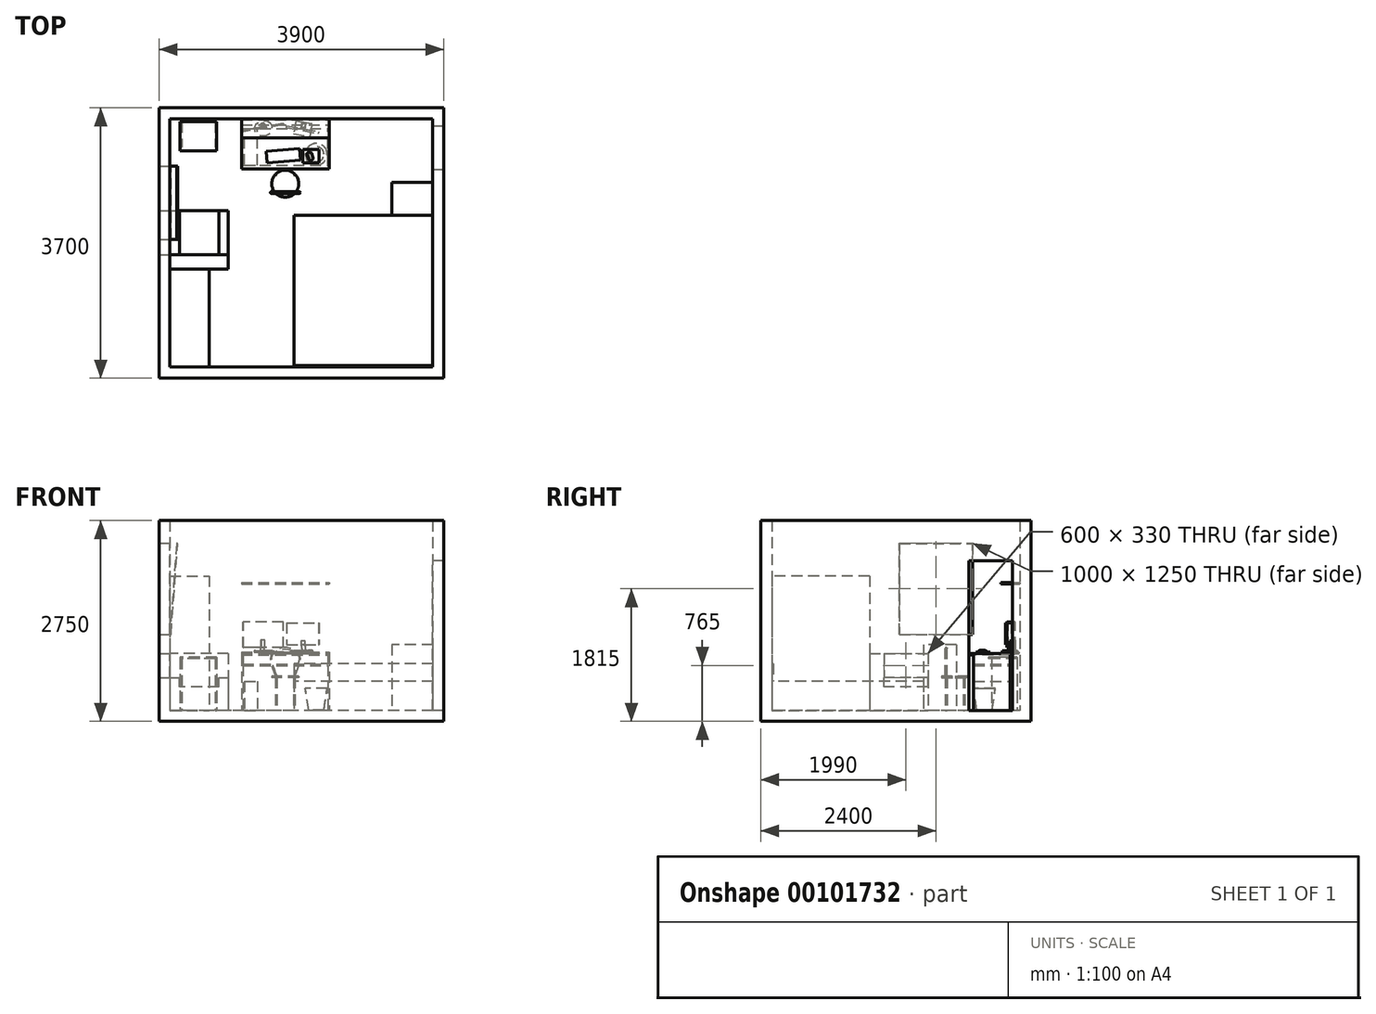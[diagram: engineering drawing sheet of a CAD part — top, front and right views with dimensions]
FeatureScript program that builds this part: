
annotation { "Feature Type Name" : "Feature", "Feature Type Description" : "" }
export const myFeature = defineFeature(function(context is Context, id is Id, definition is map)
    precondition{}
    {
        {
            var Q0;
            Q0=qCreatedBy(makeId("Top.planeOp"),FACE);
            var sketch = newSketch(context, id + "F0", { "sketchPlane" : qUnion([Q0])});
            skLineSegment(sketch, "E0.bottom", {"start": v(1800, 1700) * mm, "end": v(-1800, 1700) * mm});
            skLineSegment(sketch, "E0.top", {"start": v(1800, -1700) * mm, "end": v(-1800, -1700) * mm});
            skLineSegment(sketch, "E0.left", {"start": v(1800, 1700) * mm, "end": v(1800, -1700) * mm});
            skLineSegment(sketch, "E0.right", {"start": v(-1800, 1700) * mm, "end": v(-1800, -1700) * mm});
            skPoint(sketch, "E0.middle", {"position": v(0, 0) * mm});
            skLineSegment(sketch, "E1.0", {"start": v(-1950, 1850) * mm, "end": v(-1950, -1850) * mm});
            skLineSegment(sketch, "E1.1", {"start": v(1950, 1850) * mm, "end": v(-1950, 1850) * mm});
            skLineSegment(sketch, "E1.2", {"start": v(1950, 1850) * mm, "end": v(1950, -1850) * mm});
            skLineSegment(sketch, "E1.3", {"start": v(1950, -1850) * mm, "end": v(-1950, -1850) * mm});
            skSolve(sketch);
        }
        {
            var Q0;
            Q0 = qSketchRegion(id + "F0", true);
            var Q1;
            Q1=makeQuery(id+"F0.imprint","IMPRINT",FACE,{"disambiguationData":[TD([[makeQuery(id+"F0.imprint","IMPRINT",EDGE,{"derivedFrom":sQuery(id+"F0.wireOp",EDGE,"E0.bottom")}),1.0]])]});
            extrude(context, id + "F1", {"entities" : qUnion([Q0, Q1]), "oppositeDirection" : true, "depth" : 150 * mm});
        }
        {
            var Q0;
            Q0=makeQuery(id+"F0.imprint","IMPRINT",FACE,{"disambiguationData":[TD([[makeQuery(id+"F0.imprint","IMPRINT",EDGE,{"derivedFrom":sQuery(id+"F0.wireOp",EDGE,"E0.bottom")}),-1.0]])]});
            extrude(context, id + "F2", {"entities" : qUnion([Q0]), "operationType" : NewBodyOperationType.ADD, "depth" : 2600 * mm});
        }
        {
            var Q0;
            Q0=makeQuery(id+"F1.opExtrude","CAP_FACE",FACE,{"disambiguationData":[OSD([sQuery(id+"F0.wireOp",EDGE,"E1.0"),sQuery(id+"F0.wireOp",EDGE,"E1.1"),sQuery(id+"F0.wireOp",EDGE,"E1.2"),sQuery(id+"F0.wireOp",EDGE,"E1.3")])],"isStart":true});
            var sketch = newSketch(context, id + "F3", { "sketchPlane" : qUnion([Q0])});
            skLineSegment(sketch, "E2.bottom", {"start": v(1800, -1700) * mm, "end": v(-100, -1700) * mm});
            skLineSegment(sketch, "E2.top", {"start": v(1800, 380) * mm, "end": v(-100, 380) * mm});
            skLineSegment(sketch, "E2.left", {"start": v(1800, -1700) * mm, "end": v(1800, 380) * mm});
            skLineSegment(sketch, "E2.right", {"start": v(-100, -1700) * mm, "end": v(-100, 380) * mm});
            skSolve(sketch);
        }
        {
            var Q0;
            Q0 = qSketchRegion(id + "F3", true);
            extrude(context, id + "F4", {"entities" : qUnion([Q0]), "depth" : 400 * mm});
        }
        {
            var Q0;
            Q0=makeQuery(id+"F1.opExtrude","CAP_FACE",FACE,{"disambiguationData":[OSD([sQuery(id+"F0.wireOp",EDGE,"E1.0"),sQuery(id+"F0.wireOp",EDGE,"E1.1"),sQuery(id+"F0.wireOp",EDGE,"E1.2"),sQuery(id+"F0.wireOp",EDGE,"E1.3")])],"isStart":true});
            var sketch = newSketch(context, id + "F5", { "sketchPlane" : qUnion([Q0])});
            skLineSegment(sketch, "E3.bottom", {"start": v(-1800, -1700) * mm, "end": v(-1260, -1700) * mm});
            skLineSegment(sketch, "E3.top", {"start": v(-1800, -360) * mm, "end": v(-1260, -360) * mm});
            skLineSegment(sketch, "E3.left", {"start": v(-1800, -1700) * mm, "end": v(-1800, -360) * mm});
            skLineSegment(sketch, "E3.right", {"start": v(-1260, -1700) * mm, "end": v(-1260, -360) * mm});
            skSolve(sketch);
        }
        {
            var Q0;
            Q0 = qSketchRegion(id + "F5", true);
            extrude(context, id + "F6", {"entities" : qUnion([Q0]), "depth" : 1840 * mm});
        }
        {
            var Q0;
            Q0=makeQuery(id+"F1.opExtrude","CAP_FACE",FACE,{"disambiguationData":[OSD([sQuery(id+"F0.wireOp",EDGE,"E1.0"),sQuery(id+"F0.wireOp",EDGE,"E1.1"),sQuery(id+"F0.wireOp",EDGE,"E1.2"),sQuery(id+"F0.wireOp",EDGE,"E1.3")])],"isStart":true});
            var sketch = newSketch(context, id + "F7", { "sketchPlane" : qUnion([Q0])});
            skLineSegment(sketch, "E4.bottom", {"start": v(1800, 380) * mm, "end": v(1240, 380) * mm});
            skLineSegment(sketch, "E4.top", {"start": v(1800, 830) * mm, "end": v(1240, 830) * mm});
            skLineSegment(sketch, "E4.left", {"start": v(1800, 380) * mm, "end": v(1800, 830) * mm});
            skLineSegment(sketch, "E4.right", {"start": v(1240, 380) * mm, "end": v(1240, 830) * mm});
            skSolve(sketch);
        }
        {
            var Q0;
            Q0 = qSketchRegion(id + "F7", true);
            extrude(context, id + "F8", {"entities" : qUnion([Q0]), "depth" : 900 * mm});
        }
        {
            var Q0;
            Q0=makeQuery(id+"F1.opExtrude","CAP_FACE",FACE,{"disambiguationData":[OSD([sQuery(id+"F0.wireOp",EDGE,"E1.0"),sQuery(id+"F0.wireOp",EDGE,"E1.1"),sQuery(id+"F0.wireOp",EDGE,"E1.2"),sQuery(id+"F0.wireOp",EDGE,"E1.3")])],"isStart":true});
            var sketch = newSketch(context, id + "F9", { "sketchPlane" : qUnion([Q0])});
            skLineSegment(sketch, "E5.bottom", {"start": v(-1000, -360) * mm, "end": v(-1800, -360) * mm});
            skLineSegment(sketch, "E5.top", {"start": v(-1000, 440) * mm, "end": v(-1800, 440) * mm});
            skLineSegment(sketch, "E5.left", {"start": v(-1000, -360) * mm, "end": v(-1000, 440) * mm});
            skLineSegment(sketch, "E5.right", {"start": v(-1800, -360) * mm, "end": v(-1800, 440) * mm});
            skSolve(sketch);
        }
        {
            var Q0;
            Q0 = qSketchRegion(id + "F9", true);
            extrude(context, id + "F10", {"entities" : qUnion([Q0]), "depth" : 780 * mm});
        }
        {
            var Q0;
            Q0=makeQuery(id+"F10.opExtrude","CAP_FACE",FACE,{"disambiguationData":[OSD([sQuery(id+"F9.wireOp",EDGE,"E5.bottom"),sQuery(id+"F9.wireOp",EDGE,"E5.top"),sQuery(id+"F9.wireOp",EDGE,"E5.left"),sQuery(id+"F9.wireOp",EDGE,"E5.right")])],"isStart":false});
            var sketch = newSketch(context, id + "F11", { "sketchPlane" : qUnion([Q0])});
            skLineSegment(sketch, "E6.bottom", {"start": v(-1670, 440) * mm, "end": v(-1130, 440) * mm});
            skLineSegment(sketch, "E6.top", {"start": v(-1670, -160) * mm, "end": v(-1130, -160) * mm});
            skLineSegment(sketch, "E6.left", {"start": v(-1670, 440) * mm, "end": v(-1670, -160) * mm});
            skLineSegment(sketch, "E6.right", {"start": v(-1130, 440) * mm, "end": v(-1130, -160) * mm});
            skSolve(sketch);
        }
        {
            var Q0;
            Q0 = qSketchRegion(id + "F11", true);
            extrude(context, id + "F12", {"entities" : qUnion([Q0]), "operationType" : NewBodyOperationType.REMOVE, "oppositeDirection" : true, "depth" : 460 * mm});
        }
        {
            var Q0;
            Q0=makeQuery(id+"F12.boolean.opBoolean","COPY",FACE,{"derivedFrom":makeQuery(id+"F12.opExtrude","SWEPT_FACE",FACE,{"disambiguationData":[OSD([sQuery(id+"F11.wireOp",EDGE,"E6.left")])]})});
            var sketch = newSketch(context, id + "F13", { "sketchPlane" : qUnion([Q0])});
            skLineSegment(sketch, "E7.bottom", {"start": v(-160, 780) * mm, "end": v(440, 780) * mm});
            skLineSegment(sketch, "E7.top", {"start": v(-160, 450) * mm, "end": v(440, 450) * mm});
            skLineSegment(sketch, "E7.left", {"start": v(-160, 780) * mm, "end": v(-160, 450) * mm});
            skLineSegment(sketch, "E7.right", {"start": v(440, 780) * mm, "end": v(440, 450) * mm});
            skSolve(sketch);
        }
        {
            var Q0;
            Q0 = qSketchRegion(id + "F13", true);
            extrude(context, id + "F14", {"entities" : qUnion([Q0]), "operationType" : NewBodyOperationType.REMOVE, "oppositeDirection" : true, "depth" : 3679.97 * mm, "symmetric" : true});
        }
        {
            var Q0;
            Q0=makeQuery(id+"F2.opExtrude","SWEPT_FACE",FACE,{"disambiguationData":[OSD([sQuery(id+"F0.wireOp",EDGE,"E0.left")])]});
            var sketch = newSketch(context, id + "F15", { "sketchPlane" : qUnion([Q0])});
            skLineSegment(sketch, "E8.bottom", {"start": v(-1600, 0) * mm, "end": v(-1000, 0) * mm});
            skLineSegment(sketch, "E8.top", {"start": v(-1600, 2050) * mm, "end": v(-1000, 2050) * mm});
            skLineSegment(sketch, "E8.left", {"start": v(-1600, 0) * mm, "end": v(-1600, 2050) * mm});
            skLineSegment(sketch, "E8.right", {"start": v(-1000, 0) * mm, "end": v(-1000, 2050) * mm});
            skSolve(sketch);
        }
        {
            var Q0;
            Q0 = qSketchRegion(id + "F15", true);
            extrude(context, id + "F16", {"entities" : qUnion([Q0]), "operationType" : NewBodyOperationType.REMOVE, "oppositeDirection" : true, "depth" : 500 * mm});
        }
        {
            var Q0;
            Q0=makeQuery(id+"F16.boolean.opBoolean","MERGE",FACE,{"derivedFrom":[makeQuery(id+"F1.opExtrude","CAP_FACE",FACE,{"disambiguationData":[OSD([sQuery(id+"F0.wireOp",EDGE,"E1.0"),sQuery(id+"F0.wireOp",EDGE,"E1.1"),sQuery(id+"F0.wireOp",EDGE,"E1.2"),sQuery(id+"F0.wireOp",EDGE,"E1.3")])],"isStart":true}),makeQuery(id+"F16.opExtrude","SWEPT_FACE",FACE,{"disambiguationData":[OSD([sQuery(id+"F15.wireOp",EDGE,"E8.bottom")])]})]});
            var sketch = newSketch(context, id + "F17", { "sketchPlane" : qUnion([Q0])});
            skLineSegment(sketch, "E9.bottom", {"start": v(380, 1565) * mm, "end": v(360, 1565) * mm});
            skLineSegment(sketch, "E9.top", {"start": v(380, 1065) * mm, "end": v(360, 1065) * mm});
            skLineSegment(sketch, "E9.left", {"start": v(380, 1565) * mm, "end": v(380, 1065) * mm});
            skLineSegment(sketch, "E9.right", {"start": v(360, 1565) * mm, "end": v(360, 1065) * mm});
            skLineSegment(sketch, "E10.bottom", {"start": v(-800, 1565) * mm, "end": v(-820, 1565) * mm});
            skLineSegment(sketch, "E10.top", {"start": v(-800, 1065) * mm, "end": v(-820, 1065) * mm});
            skLineSegment(sketch, "E10.left", {"start": v(-800, 1565) * mm, "end": v(-800, 1065) * mm});
            skLineSegment(sketch, "E10.right", {"start": v(-820, 1565) * mm, "end": v(-820, 1065) * mm});
            skSolve(sketch);
        }
        {
            var Q0;
            Q0 = qSketchRegion(id + "F17", true);
            extrude(context, id + "F18", {"entities" : qUnion([Q0]), "depth" : 760 * mm});
        }
        {
            var Q0;
            Q0=makeQuery(id+"F18.opExtrude","CAP_FACE",FACE,{"disambiguationData":[OSD([sQuery(id+"F17.wireOp",EDGE,"E10.bottom"),sQuery(id+"F17.wireOp",EDGE,"E10.top"),sQuery(id+"F17.wireOp",EDGE,"E10.left"),sQuery(id+"F17.wireOp",EDGE,"E10.right")])],"isStart":false});
            var sketch = newSketch(context, id + "F19", { "sketchPlane" : qUnion([Q0])});
            skLineSegment(sketch, "E11.bottom", {"start": v(-820, 1615) * mm, "end": v(380, 1615) * mm});
            skLineSegment(sketch, "E11.top", {"start": v(-820, 1015) * mm, "end": v(380, 1015) * mm});
            skLineSegment(sketch, "E11.left", {"start": v(-820, 1615) * mm, "end": v(-820, 1015) * mm});
            skLineSegment(sketch, "E11.right", {"start": v(380, 1615) * mm, "end": v(380, 1015) * mm});
            skSolve(sketch);
        }
        {
            var Q0;
            Q0 = qSketchRegion(id + "F19", true);
            extrude(context, id + "F20", {"entities" : qUnion([Q0]), "operationType" : NewBodyOperationType.ADD, "depth" : 20 * mm});
        }
        {
            var Q0;
            Q0=makeQuery(id+"F20.opExtrude","CAP_FACE",FACE,{"disambiguationData":[OSD([sQuery(id+"F19.wireOp",EDGE,"E11.bottom"),sQuery(id+"F19.wireOp",EDGE,"E11.top"),sQuery(id+"F19.wireOp",EDGE,"E11.left"),sQuery(id+"F19.wireOp",EDGE,"E11.right")])],"isStart":true});
            cPlane(context, id + "F21", {"entities" : qUnion([Q0]), "cplaneType" : CPlaneType.OFFSET, "offset" : 125 * mm, "width" : 150 * mm, "height" : 150 * mm});
        }
        {
            var Q0;
            Q0=qCreatedBy(id+"F21.planeOp",FACE);
            var sketch = newSketch(context, id + "F22", { "sketchPlane" : qUnion([Q0])});
            skLineSegment(sketch, "E12.bottom", {"start": v(-800, -1065) * mm, "end": v(360, -1065) * mm});
            skLineSegment(sketch, "E12.top", {"start": v(-800, -1565) * mm, "end": v(360, -1565) * mm});
            skLineSegment(sketch, "E12.left", {"start": v(-800, -1065) * mm, "end": v(-800, -1565) * mm});
            skLineSegment(sketch, "E12.right", {"start": v(360, -1065) * mm, "end": v(360, -1565) * mm});
            skSolve(sketch);
        }
        {
            var Q0;
            Q0 = qSketchRegion(id + "F22", true);
            extrude(context, id + "F23", {"entities" : qUnion([Q0]), "operationType" : NewBodyOperationType.ADD, "depth" : 20 * mm});
        }
        {
            var Q0;
            Q0=makeQuery(id+"F20.opExtrude","CAP_FACE",FACE,{"disambiguationData":[OSD([sQuery(id+"F19.wireOp",EDGE,"E11.bottom"),sQuery(id+"F19.wireOp",EDGE,"E11.top"),sQuery(id+"F19.wireOp",EDGE,"E11.left"),sQuery(id+"F19.wireOp",EDGE,"E11.right")])],"isStart":false});
            var sketch = newSketch(context, id + "F24", { "sketchPlane" : qUnion([Q0])});
            skLineSegment(sketch, "E13.bottom", {"start": v(-820, 1440) * mm, "end": v(380, 1440) * mm});
            skLineSegment(sketch, "E13.top", {"start": v(-820, 1690) * mm, "end": v(380, 1690) * mm});
            skLineSegment(sketch, "E13.left", {"start": v(-820, 1440) * mm, "end": v(-820, 1690) * mm});
            skLineSegment(sketch, "E13.right", {"start": v(380, 1440) * mm, "end": v(380, 1690) * mm});
            skSolve(sketch);
        }
        {
            var Q0;
            Q0 = qSketchRegion(id + "F24", true);
            extrude(context, id + "F25", {"entities" : qUnion([Q0]), "operationType" : NewBodyOperationType.ADD, "depth" : 20 * mm});
        }
        {
            var Q0;
            Q0=makeQuery(id+"F16.boolean.opBoolean","MERGE",FACE,{"derivedFrom":[makeQuery(id+"F1.opExtrude","CAP_FACE",FACE,{"disambiguationData":[OSD([sQuery(id+"F0.wireOp",EDGE,"E1.0"),sQuery(id+"F0.wireOp",EDGE,"E1.1"),sQuery(id+"F0.wireOp",EDGE,"E1.2"),sQuery(id+"F0.wireOp",EDGE,"E1.3")])],"isStart":true}),makeQuery(id+"F16.opExtrude","SWEPT_FACE",FACE,{"disambiguationData":[OSD([sQuery(id+"F15.wireOp",EDGE,"E8.bottom")])]})]});
            var sketch = newSketch(context, id + "F26", { "sketchPlane" : qUnion([Q0])});
            skLineSegment(sketch, "E14.bottom", {"start": v(-1180, 1660) * mm, "end": v(-1160, 1660) * mm});
            skLineSegment(sketch, "E14.top", {"start": v(-1180, 1315) * mm, "end": v(-1160, 1315) * mm});
            skLineSegment(sketch, "E14.left", {"start": v(-1180, 1660) * mm, "end": v(-1180, 1315) * mm});
            skLineSegment(sketch, "E14.right", {"start": v(-1160, 1660) * mm, "end": v(-1160, 1315) * mm});
            skLineSegment(sketch, "E15.bottom", {"start": v(-1660, 1660) * mm, "end": v(-1640, 1660) * mm});
            skLineSegment(sketch, "E15.top", {"start": v(-1660, 1315) * mm, "end": v(-1640, 1315) * mm});
            skLineSegment(sketch, "E15.left", {"start": v(-1660, 1660) * mm, "end": v(-1660, 1315) * mm});
            skLineSegment(sketch, "E15.right", {"start": v(-1640, 1660) * mm, "end": v(-1640, 1315) * mm});
            skSolve(sketch);
        }
        {
            var Q0;
            Q0 = qSketchRegion(id + "F26", true);
            extrude(context, id + "F27", {"entities" : qUnion([Q0]), "depth" : 710 * mm});
        }
        {
            var Q0;
            Q0=makeQuery(id+"F4.opExtrude","CAP_FACE",FACE,{"disambiguationData":[OSD([sQuery(id+"F3.wireOp",EDGE,"E2.bottom"),sQuery(id+"F3.wireOp",EDGE,"E2.top"),sQuery(id+"F3.wireOp",EDGE,"E2.left"),sQuery(id+"F3.wireOp",EDGE,"E2.right")])],"isStart":false});
            var sketch = newSketch(context, id + "F28", { "sketchPlane" : qUnion([Q0])});
            skLineSegment(sketch, "E16.bottom", {"start": v(1800, -1700) * mm, "end": v(-100, -1700) * mm});
            skLineSegment(sketch, "E16.top", {"start": v(1800, -1680) * mm, "end": v(-100, -1680) * mm});
            skLineSegment(sketch, "E16.left", {"start": v(1800, -1700) * mm, "end": v(1800, -1680) * mm});
            skLineSegment(sketch, "E16.right", {"start": v(-100, -1700) * mm, "end": v(-100, -1680) * mm});
            skSolve(sketch);
        }
        {
            var Q0;
            Q0 = qSketchRegion(id + "F28", true);
            extrude(context, id + "F29", {"entities" : qUnion([Q0]), "operationType" : NewBodyOperationType.ADD, "depth" : 240 * mm});
        }
        {
            var Q0;
            Q0=makeQuery(id+"F27.opExtrude","CAP_FACE",FACE,{"disambiguationData":[OSD([sQuery(id+"F26.wireOp",EDGE,"E14.bottom"),sQuery(id+"F26.wireOp",EDGE,"E14.top"),sQuery(id+"F26.wireOp",EDGE,"E14.left"),sQuery(id+"F26.wireOp",EDGE,"E14.right")])],"isStart":false});
            var sketch = newSketch(context, id + "F30", { "sketchPlane" : qUnion([Q0])});
            skLineSegment(sketch, "E17.bottom", {"start": v(-1160, 1660) * mm, "end": v(-1660, 1660) * mm});
            skLineSegment(sketch, "E17.top", {"start": v(-1160, 1265) * mm, "end": v(-1660, 1265) * mm});
            skLineSegment(sketch, "E17.left", {"start": v(-1160, 1660) * mm, "end": v(-1160, 1265) * mm});
            skLineSegment(sketch, "E17.right", {"start": v(-1660, 1660) * mm, "end": v(-1660, 1265) * mm});
            skSolve(sketch);
        }
        {
            var Q0;
            Q0 = qSketchRegion(id + "F30", true);
            extrude(context, id + "F31", {"entities" : qUnion([Q0]), "operationType" : NewBodyOperationType.ADD, "depth" : 20 * mm});
        }
        {
            var Q0;
            Q0=makeQuery(id+"F2.opExtrude","SWEPT_FACE",FACE,{"disambiguationData":[OSD([sQuery(id+"F0.wireOp",EDGE,"E0.bottom")])]});
            var sketch = newSketch(context, id + "F32", { "sketchPlane" : qUnion([Q0])});
            skLineSegment(sketch, "E18.bottom", {"start": v(-820, 1750) * mm, "end": v(380, 1750) * mm});
            skLineSegment(sketch, "E18.top", {"start": v(-820, 1730) * mm, "end": v(380, 1730) * mm});
            skLineSegment(sketch, "E18.left", {"start": v(-820, 1750) * mm, "end": v(-820, 1730) * mm});
            skLineSegment(sketch, "E18.right", {"start": v(380, 1750) * mm, "end": v(380, 1730) * mm});
            skSolve(sketch);
        }
        {
            var Q0;
            Q0 = qSketchRegion(id + "F32", true);
            extrude(context, id + "F33", {"entities" : qUnion([Q0]), "depth" : 260 * mm});
        }
        {
            var Q0;
            Q0=makeQuery(id+"F2.opExtrude","SWEPT_FACE",FACE,{"disambiguationData":[OSD([sQuery(id+"F0.wireOp",EDGE,"E0.right")])]});
            var sketch = newSketch(context, id + "F34", { "sketchPlane" : qUnion([Q0])});
            skLineSegment(sketch, "E19.bottom", {"start": v(1050, 1040) * mm, "end": v(50, 1040) * mm});
            skLineSegment(sketch, "E19.top", {"start": v(1050, 2290) * mm, "end": v(50, 2290) * mm});
            skLineSegment(sketch, "E19.left", {"start": v(1050, 1040) * mm, "end": v(1050, 2290) * mm});
            skLineSegment(sketch, "E19.right", {"start": v(50, 1040) * mm, "end": v(50, 2290) * mm});
            skSolve(sketch);
        }
        {
            var Q0;
            Q0 = qSketchRegion(id + "F34", true);
            extrude(context, id + "F35", {"entities" : qUnion([Q0]), "operationType" : NewBodyOperationType.REMOVE, "oppositeDirection" : true, "depth" : 500 * mm});
        }
        {
            var Q0;
            Q0=makeQuery(id+"F2.opExtrude","CAP_FACE",FACE,{"disambiguationData":[OSD([sQuery(id+"F0.wireOp",EDGE,"E0.bottom"),sQuery(id+"F0.wireOp",EDGE,"E0.top"),sQuery(id+"F0.wireOp",EDGE,"E0.left"),sQuery(id+"F0.wireOp",EDGE,"E0.right"),sQuery(id+"F0.wireOp",EDGE,"E1.0"),sQuery(id+"F0.wireOp",EDGE,"E1.1"),sQuery(id+"F0.wireOp",EDGE,"E1.2"),sQuery(id+"F0.wireOp",EDGE,"E1.3")])],"isStart":false});
            var sketch = newSketch(context, id + "F36", { "sketchPlane" : qUnion([Q0])});
            skLineSegment(sketch, "E20.0", {"start": v(-1950, 1850) * mm, "end": v(-1950, -1850) * mm});
            skLineSegment(sketch, "E20.1", {"start": v(1950, -1850) * mm, "end": v(-1950, -1850) * mm});
            skLineSegment(sketch, "E20.2", {"start": v(1950, 1850) * mm, "end": v(1950, -1850) * mm});
            skLineSegment(sketch, "E20.3", {"start": v(1950, 1850) * mm, "end": v(-1950, 1850) * mm});
            skSolve(sketch);
        }
        {
            var Q0;
            Q0=makeQuery(id+"F35.boolean.opBoolean","COPY",FACE,{"derivedFrom":makeQuery(id+"F35.opExtrude","SWEPT_FACE",FACE,{"disambiguationData":[OSD([sQuery(id+"F34.wireOp",EDGE,"E19.left")])]})});
            var sketch = newSketch(context, id + "F37", { "sketchPlane" : qUnion([Q0])});
            skLineSegment(sketch, "E21", {"start": v(-1800, 1040) * mm, "end": v(-1710, 2286.76) * mm});
            skLineSegment(sketch, "E22", {"start": v(-1710, 2286.76) * mm, "end": v(-1695.04, 2285.68) * mm});
            skLineSegment(sketch, "E23", {"start": v(-1695.04, 2285.68) * mm, "end": v(-1785.04, 1038.92) * mm});
            skLineSegment(sketch, "E24", {"start": v(-1785.04, 1038.92) * mm, "end": v(-1800, 1040) * mm});
            skSolve(sketch);
        }
        {
            var Q0;
            Q0 = qSketchRegion(id + "F37", true);
            var Q1;
            Q1=makeQuery(id+"F35.boolean.opBoolean","COPY",FACE,{"derivedFrom":makeQuery(id+"F35.opExtrude","SWEPT_FACE",FACE,{"disambiguationData":[OSD([sQuery(id+"F34.wireOp",EDGE,"E19.right")])]})});
            extrude(context, id + "F38", {"entities" : qUnion([Q0]), "endBound" : BoundingType.UP_TO_SURFACE, "endBoundEntityFace" : qUnion([Q1]), "depth" : 25 * mm});
        }
        {
            var Q0;
            Q0=makeQuery(id+"F16.boolean.opBoolean","MERGE",FACE,{"derivedFrom":[makeQuery(id+"F1.opExtrude","CAP_FACE",FACE,{"disambiguationData":[OSD([sQuery(id+"F0.wireOp",EDGE,"E1.0"),sQuery(id+"F0.wireOp",EDGE,"E1.1"),sQuery(id+"F0.wireOp",EDGE,"E1.2"),sQuery(id+"F0.wireOp",EDGE,"E1.3")])],"isStart":true}),makeQuery(id+"F16.opExtrude","SWEPT_FACE",FACE,{"disambiguationData":[OSD([sQuery(id+"F15.wireOp",EDGE,"E8.bottom")])]})]});
            var sketch = newSketch(context, id + "F39", { "sketchPlane" : qUnion([Q0])});
            skCircle(sketch, "E25", {"center": v(-342.5, 935) * mm, "radius": 10 * mm});
            skCircle(sketch, "E26", {"center": v(-97.5, 935) * mm, "radius": 10 * mm});
            skCircle(sketch, "E27", {"center": v(-97.5, 690) * mm, "radius": 10 * mm});
            skCircle(sketch, "E28", {"center": v(-342.5, 690) * mm, "radius": 10 * mm});
            skLineSegment(sketch, "E29", {"start": v(-97.5, 935) * mm, "end": v(-342.5, 935) * mm, "construction": true});
            skLineSegment(sketch, "E30", {"start": v(-220, 935) * mm, "end": v(-220, 690) * mm, "construction": true});
            skLineSegment(sketch, "E31", {"start": v(-97.5, 690) * mm, "end": v(-342.5, 690) * mm, "construction": true});
            skLineSegment(sketch, "E32", {"start": v(-220, 935) * mm, "end": v(-220, 1015) * mm, "construction": true});
            skSolve(sketch);
        }
        {
            var Q0;
            Q0 = qSketchRegion(id + "F39", true);
            extrude(context, id + "F40", {"entities" : qUnion([Q0]), "depth" : 450 * mm});
        }
        {
            var Q0;
            Q0=makeQuery(id+"F40.opExtrude","CAP_FACE",FACE,{"disambiguationData":[OSD([sQuery(id+"F39.wireOp",EDGE,"E27")])],"isStart":false});
            var sketch = newSketch(context, id + "F41", { "sketchPlane" : qUnion([Q0])});
            skCircle(sketch, "E33", {"center": v(-220, 812.5) * mm, "radius": 185 * mm});
            skSolve(sketch);
        }
        {
            var Q0;
            Q0 = qSketchRegion(id + "F41", true);
            extrude(context, id + "F42", {"entities" : qUnion([Q0]), "operationType" : NewBodyOperationType.ADD, "depth" : 20 * mm});
        }
        {
            var Q0;
            Q0=makeQuery(id+"F42.opExtrude","CAP_FACE",FACE,{"disambiguationData":[OSD([sQuery(id+"F41.wireOp",EDGE,"E33")])],"isStart":false});
            var sketch = newSketch(context, id + "F43", { "sketchPlane" : qUnion([Q0])});
            skCircle(sketch, "E34.0", {"center": v(-97.5, 690) * mm, "radius": 10 * mm});
            skCircle(sketch, "E35.0", {"center": v(-342.5, 690) * mm, "radius": 10 * mm});
            skSolve(sketch);
        }
        {
            var Q0;
            Q0=sQuery(id+"F39.wireOp",EDGE,"E31");
            var Q1;
            Q1=qCreatedBy(makeId("Front.planeOp"),FACE);
            cPlane(context, id + "F44", {"entities" : qUnion([Q0, Q1]), "cplaneType" : CPlaneType.LINE_ANGLE, "offset" : 150 * mm, "angle" : 0 * degree, "width" : 150 * mm, "height" : 150 * mm});
        }
        {
            var Q0;
            Q0=qCreatedBy(id+"F44.planeOp",FACE);
            var sketch = newSketch(context, id + "F45", { "sketchPlane" : qUnion([Q0])});
            skLineSegment(sketch, "E36", {"start": v(220, 470) * mm, "end": v(220, 850) * mm, "construction": true});
            skLineSegment(sketch, "E37", {"start": v(30, 750) * mm, "end": v(410, 750) * mm, "construction": true});
            skPoint(sketch, "E38", {"position": v(220, 750) * mm});
            skFitSpline(sketch, "E39", {"points": [v(97.5, 470) * mm, v(30, 750) * mm, v(220, 850) * mm, v(410, 750) * mm, v(342.5, 470) * mm], "startDerivative": vector(-408.08, 1106.86) * mm, "endDerivative": vector(-408.08, -1106.86) * mm});
            skSolve(sketch);
        }
        {
            var Q0;
            Q0=makeQuery(id+"F43.imprint","IMPRINT",FACE,{"disambiguationData":[TD([[makeQuery(id+"F43.imprint","IMPRINT",EDGE,{"derivedFrom":sQuery(id+"F43.wireOp",EDGE,"E34.0")}),1.0]])]});
            var Q1;
            Q1=sQuery(id+"F45.wireOp",EDGE,"E39");
            sweep(context, id + "F46", {"operationType" : NewBodyOperationType.ADD, "profiles" : qUnion([Q0]), "path" : qUnion([Q1])});
        }
        {
            var Q0;
            Q0=makeQuery(id+"F25.opExtrude","CAP_FACE",FACE,{"disambiguationData":[OSD([sQuery(id+"F24.wireOp",EDGE,"E13.bottom"),sQuery(id+"F24.wireOp",EDGE,"E13.top"),sQuery(id+"F24.wireOp",EDGE,"E13.left"),sQuery(id+"F24.wireOp",EDGE,"E13.right")])],"isStart":false});
            var sketch = newSketch(context, id + "F47", { "sketchPlane" : qUnion([Q0])});
            skEllipse(sketch, "E40", {"center": v(-520, 1570) * mm, "majorRadius": 125 * mm, "minorRadius": 100 * mm, "majorAxis": v(0.98, 0.17)});
            skLineSegment(sketch, "E41", {"start": v(-520, 1570) * mm, "end": v(-396.9, 1591.7) * mm, "construction": true});
            skSolve(sketch);
        }
        {
            var Q0;
            Q0 = qSketchRegion(id + "F47", true);
            extrude(context, id + "F48", {"entities" : qUnion([Q0]), "depth" : 15 * mm});
        }
        {
            var Q0;
            Q0=makeQuery(id+"F48.opExtrude","CAP_FACE",FACE,{"disambiguationData":[OSD([sQuery(id+"F47.wireOp",EDGE,"E40")])],"isStart":false});
            var sketch = newSketch(context, id + "F49", { "sketchPlane" : qUnion([Q0])});
            skEllipse(sketch, "E42", {"center": v(-530.42, 1629.09) * mm, "majorRadius": 25 * mm, "minorRadius": 10 * mm, "majorAxis": v(0.98, 0.17)});
            skLineSegment(sketch, "E43", {"start": v(-643.1, 1548.3) * mm, "end": v(-396.9, 1591.7) * mm, "construction": true});
            skLineSegment(sketch, "E44", {"start": v(-537.36, 1668.48) * mm, "end": v(-502.64, 1471.52) * mm, "construction": true});
            skLineSegment(sketch, "E45", {"start": v(-505.8, 1633.43) * mm, "end": v(-530.42, 1629.09) * mm, "construction": true});
            skPoint(sketch, "E46", {"position": v(-520, 1570) * mm});
            skSolve(sketch);
        }
        {
            var Q0;
            Q0 = qSketchRegion(id + "F49", true);
            extrude(context, id + "F50", {"entities" : qUnion([Q0]), "operationType" : NewBodyOperationType.ADD, "depth" : 150 * mm});
        }
        {
            var Q0;
            Q0=sQuery(id+"F49.wireOp",EDGE,"E44");
            cPlane(context, id + "F51", {"entities" : qUnion([Q0]), "cplaneType" : CPlaneType.MID_PLANE, "offset" : 150 * mm, "width" : 150 * mm, "height" : 150 * mm});
        }
        {
            var Q0;
            Q0=qCreatedBy(id+"F51.planeOp",FACE);
            var sketch = newSketch(context, id + "F52", { "sketchPlane" : qUnion([Q0])});
            skLineSegment(sketch, "E47.bottom", {"start": v(40.53, 860) * mm, "end": v(-519.47, 860) * mm});
            skLineSegment(sketch, "E47.top", {"start": v(40.53, 1210) * mm, "end": v(-519.47, 1210) * mm});
            skLineSegment(sketch, "E47.left", {"start": v(40.53, 860) * mm, "end": v(40.53, 1210) * mm});
            skLineSegment(sketch, "E47.right", {"start": v(-519.47, 860) * mm, "end": v(-519.47, 1210) * mm});
            skLineSegment(sketch, "E48", {"start": v(-239.47, 860) * mm, "end": v(-239.47, 815) * mm, "construction": true});
            skSolve(sketch);
        }
        {
            var Q0;
            Q0=makeQuery(id+"F52.imprint","IMPRINT",FACE,{"disambiguationData":[TD([[makeQuery(id+"F52.imprint","IMPRINT",EDGE,{"derivedFrom":sQuery(id+"F52.wireOp",EDGE,"E47.bottom")}),-1.0]])]});
            var Q1;
            Q1=sQuery(id+"F52.wireOp",EDGE,"E47.right");
            var Q2;
            Q2=sQuery(id+"F52.wireOp",EDGE,"E47.bottom");
            var Q3;
            Q3=sQuery(id+"F52.wireOp",EDGE,"E47.left");
            var Q4;
            Q4=sQuery(id+"F52.wireOp",EDGE,"E47.top");
            extrude(context, id + "F53", {"entities" : qUnion([Q0]), "operationType" : NewBodyOperationType.ADD, "surfaceEntities" : qUnion([Q1, Q2, Q3, Q4]), "oppositeDirection" : true, "depth" : 20 * mm});
        }
        {
            var Q0;
            Q0=sQuery(id+"F49.wireOp",EDGE,"E43");
            cPlane(context, id + "F54", {"entities" : qUnion([Q0]), "cplaneType" : CPlaneType.MID_PLANE, "offset" : 150 * mm, "width" : 150 * mm, "height" : 150 * mm});
        }
        {
            var Q0;
            Q0=qCreatedBy(id+"F54.planeOp",FACE);
            var sketch = newSketch(context, id + "F55", { "sketchPlane" : qUnion([Q0])});
            skLineSegment(sketch, "E49", {"start": v(1656.45, 965) * mm, "end": v(1699.45, 965) * mm});
            skLineSegment(sketch, "E50", {"start": v(1699.45, 965) * mm, "end": v(1699.45, 860) * mm});
            skLineSegment(sketch, "E51", {"start": v(1699.45, 860) * mm, "end": v(1656.45, 860) * mm});
            skLineSegment(sketch, "E52", {"start": v(1656.45, 860) * mm, "end": v(1656.45, 965) * mm});
            skSolve(sketch);
        }
        {
            var Q0;
            Q0 = qSketchRegion(id + "F55", true);
            extrude(context, id + "F56", {"entities" : qUnion([Q0]), "operationType" : NewBodyOperationType.ADD, "depth" : 50 * mm, "symmetric" : true});
        }
        {
            var Q0;
            Q0=makeQuery(id+"F25.opExtrude","CAP_FACE",FACE,{"disambiguationData":[OSD([sQuery(id+"F24.wireOp",EDGE,"E13.bottom"),sQuery(id+"F24.wireOp",EDGE,"E13.top"),sQuery(id+"F24.wireOp",EDGE,"E13.left"),sQuery(id+"F24.wireOp",EDGE,"E13.right")])],"isStart":false});
            var sketch = newSketch(context, id + "F57", { "sketchPlane" : qUnion([Q0])});
            skLineSegment(sketch, "E53", {"start": v(149.52, 1627.42) * mm, "end": v(-76.99, 1667.36) * mm});
            skLineSegment(sketch, "E54", {"start": v(-76.99, 1667.36) * mm, "end": v(-106.5, 1499.94) * mm});
            skLineSegment(sketch, "E55", {"start": v(-106.5, 1499.94) * mm, "end": v(120, 1460) * mm});
            skLineSegment(sketch, "E56", {"start": v(120, 1460) * mm, "end": v(149.52, 1627.42) * mm});
            skLineSegment(sketch, "E57", {"start": v(36.27, 1647.39) * mm, "end": v(6.75, 1479.97) * mm, "construction": true});
            skLineSegment(sketch, "E58", {"start": v(-91.75, 1583.65) * mm, "end": v(134.76, 1543.7) * mm, "construction": true});
            skSolve(sketch);
        }
        {
            var Q0;
            Q0 = qSketchRegion(id + "F57", true);
            extrude(context, id + "F58", {"entities" : qUnion([Q0]), "depth" : 15 * mm});
        }
        {
            var Q0;
            Q0=sQuery(id+"F57.wireOp",EDGE,"E58");
            cPlane(context, id + "F59", {"entities" : qUnion([Q0]), "cplaneType" : CPlaneType.MID_PLANE, "offset" : 150 * mm, "width" : 150 * mm, "height" : 150 * mm});
        }
        {
            var Q0;
            Q0=sQuery(id+"F57.wireOp",EDGE,"E57");
            cPlane(context, id + "F60", {"entities" : qUnion([Q0]), "cplaneType" : CPlaneType.MID_PLANE, "offset" : 150 * mm, "width" : 150 * mm, "height" : 150 * mm});
        }
        {
            var Q0;
            Q0=qCreatedBy(id+"F60.planeOp",FACE);
            var sketch = newSketch(context, id + "F61", { "sketchPlane" : qUnion([Q0])});
            skLineSegment(sketch, "E59.bottom", {"start": v(-475.35, 1200) * mm, "end": v(-25.35, 1200) * mm});
            skLineSegment(sketch, "E59.top", {"start": v(-475.35, 900) * mm, "end": v(-25.35, 900) * mm});
            skLineSegment(sketch, "E59.left", {"start": v(-475.35, 1200) * mm, "end": v(-475.35, 900) * mm});
            skLineSegment(sketch, "E59.right", {"start": v(-25.35, 1200) * mm, "end": v(-25.35, 900) * mm});
            skLineSegment(sketch, "E60", {"start": v(-250.35, 900) * mm, "end": v(-250.35, 800) * mm, "construction": true});
            skSolve(sketch);
        }
        {
            var Q0;
            Q0 = qSketchRegion(id + "F61", true);
            extrude(context, id + "F62", {"entities" : qUnion([Q0]), "depth" : 25 * mm});
        }
        {
            var Q0;
            Q0=qCreatedBy(id+"F59.planeOp",FACE);
            var sketch = newSketch(context, id + "F63", { "sketchPlane" : qUnion([Q0])});
            skLineSegment(sketch, "E61", {"start": v(1543.66, 950) * mm, "end": v(1543.66, 900) * mm});
            skLineSegment(sketch, "E62", {"start": v(1543.66, 900) * mm, "end": v(1608.66, 815) * mm});
            skLineSegment(sketch, "E63", {"start": v(1608.66, 815) * mm, "end": v(1628.66, 815) * mm});
            skLineSegment(sketch, "E64", {"start": v(1628.66, 815) * mm, "end": v(1563.66, 950) * mm});
            skLineSegment(sketch, "E65", {"start": v(1563.66, 950) * mm, "end": v(1543.66, 950) * mm});
            skSolve(sketch);
        }
        {
            var Q0;
            Q0 = qSketchRegion(id + "F63", true);
            extrude(context, id + "F64", {"entities" : qUnion([Q0]), "operationType" : NewBodyOperationType.ADD, "depth" : 50 * mm, "symmetric" : true});
        }
        {
            var Q0;
            Q0=makeQuery(id+"F16.boolean.opBoolean","MERGE",FACE,{"derivedFrom":[makeQuery(id+"F1.opExtrude","CAP_FACE",FACE,{"disambiguationData":[OSD([sQuery(id+"F0.wireOp",EDGE,"E1.0"),sQuery(id+"F0.wireOp",EDGE,"E1.1"),sQuery(id+"F0.wireOp",EDGE,"E1.2"),sQuery(id+"F0.wireOp",EDGE,"E1.3")])],"isStart":true}),makeQuery(id+"F16.opExtrude","SWEPT_FACE",FACE,{"disambiguationData":[OSD([sQuery(id+"F15.wireOp",EDGE,"E8.bottom")])]})]});
            var sketch = newSketch(context, id + "F65", { "sketchPlane" : qUnion([Q0])});
            skCircle(sketch, "E66", {"center": v(205, 1215) * mm, "radius": 105 * mm});
            skCircle(sketch, "E67", {"center": v(205, 1215) * mm, "radius": 150 * mm, "construction": true});
            skSolve(sketch);
        }
        {
            var Q0;
            Q0=makeQuery(id+"F65.imprint","IMPRINT",FACE,{"disambiguationData":[TD([[makeQuery(id+"F65.imprint","IMPRINT",EDGE,{"derivedFrom":sQuery(id+"F65.wireOp",EDGE,"E66")}),1.0]])]});
            extrude(context, id + "F66", {"entities" : qUnion([Q0]), "depth" : 300 * mm, "hasDraft" : true, "draftAngle" : 8.53 * degree});
        }
        {
            var Q0;
            Q0=makeQuery(id+"F16.boolean.opBoolean","MERGE",FACE,{"derivedFrom":[makeQuery(id+"F1.opExtrude","CAP_FACE",FACE,{"disambiguationData":[OSD([sQuery(id+"F0.wireOp",EDGE,"E1.0"),sQuery(id+"F0.wireOp",EDGE,"E1.1"),sQuery(id+"F0.wireOp",EDGE,"E1.2"),sQuery(id+"F0.wireOp",EDGE,"E1.3")])],"isStart":true}),makeQuery(id+"F16.opExtrude","SWEPT_FACE",FACE,{"disambiguationData":[OSD([sQuery(id+"F15.wireOp",EDGE,"E8.bottom")])]})]});
            var sketch = newSketch(context, id + "F67", { "sketchPlane" : qUnion([Q0])});
            skLineSegment(sketch, "E68.bottom", {"start": v(-780, 1065) * mm, "end": v(-600, 1065) * mm});
            skLineSegment(sketch, "E68.top", {"start": v(-780, 1565) * mm, "end": v(-600, 1565) * mm});
            skLineSegment(sketch, "E68.left", {"start": v(-780, 1065) * mm, "end": v(-780, 1565) * mm});
            skLineSegment(sketch, "E68.right", {"start": v(-600, 1065) * mm, "end": v(-600, 1565) * mm});
            skSolve(sketch);
        }
        {
            var Q0;
            Q0 = qSketchRegion(id + "F67", true);
            extrude(context, id + "F68", {"entities" : qUnion([Q0]), "depth" : 400 * mm});
        }
        {
            var Q0;
            Q0=makeQuery(id+"F66.opExtrude","CAP_FACE",FACE,{"disambiguationData":[OSD([sQuery(id+"F65.wireOp",EDGE,"E66")])],"isStart":false});
            shell(context, id + "F69", {"entities" : qUnion([Q0]), "thickness" : 2.5 * mm});
        }
        {
            var Q0;
            Q0=makeQuery(id+"F20.opExtrude","CAP_FACE",FACE,{"disambiguationData":[OSD([sQuery(id+"F19.wireOp",EDGE,"E11.bottom"),sQuery(id+"F19.wireOp",EDGE,"E11.top"),sQuery(id+"F19.wireOp",EDGE,"E11.left"),sQuery(id+"F19.wireOp",EDGE,"E11.right")])],"isStart":false});
            var sketch = newSketch(context, id + "F70", { "sketchPlane" : qUnion([Q0])});
            skLineSegment(sketch, "E69", {"start": v(-470, 1095) * mm, "end": v(-483.94, 1254.4) * mm});
            skLineSegment(sketch, "E70", {"start": v(-483.94, 1254.4) * mm, "end": v(-25.7, 1294.48) * mm});
            skLineSegment(sketch, "E71", {"start": v(-25.7, 1294.48) * mm, "end": v(-11.75, 1135.1) * mm});
            skLineSegment(sketch, "E72", {"start": v(-11.75, 1135.1) * mm, "end": v(-470, 1095) * mm});
            skSolve(sketch);
        }
        {
            var Q0;
            Q0 = qSketchRegion(id + "F70", true);
            extrude(context, id + "F71", {"entities" : qUnion([Q0]), "depth" : 20 * mm});
        }
        {
            var Q0;
            Q0=makeQuery(id+"F20.opExtrude","CAP_FACE",FACE,{"disambiguationData":[OSD([sQuery(id+"F19.wireOp",EDGE,"E11.bottom"),sQuery(id+"F19.wireOp",EDGE,"E11.top"),sQuery(id+"F19.wireOp",EDGE,"E11.left"),sQuery(id+"F19.wireOp",EDGE,"E11.right")])],"isStart":false});
            var sketch = newSketch(context, id + "F72", { "sketchPlane" : qUnion([Q0])});
            skLineSegment(sketch, "E73.bottom", {"start": v(17.42, 1279.48) * mm, "end": v(242.42, 1279.48) * mm});
            skLineSegment(sketch, "E73.top", {"start": v(17.42, 1094.48) * mm, "end": v(242.42, 1094.48) * mm});
            skLineSegment(sketch, "E73.left", {"start": v(17.42, 1279.48) * mm, "end": v(17.42, 1094.48) * mm});
            skLineSegment(sketch, "E73.right", {"start": v(242.42, 1279.48) * mm, "end": v(242.42, 1094.48) * mm});
            skSolve(sketch);
        }
        {
            var Q0;
            Q0 = qSketchRegion(id + "F72", true);
            extrude(context, id + "F73", {"entities" : qUnion([Q0]), "depth" : 5 * mm});
        }
        {
            var Q0;
            Q0=makeQuery(id+"F73.opExtrude","CAP_FACE",FACE,{"disambiguationData":[OSD([sQuery(id+"F72.wireOp",EDGE,"E73.bottom"),sQuery(id+"F72.wireOp",EDGE,"E73.top"),sQuery(id+"F72.wireOp",EDGE,"E73.left"),sQuery(id+"F72.wireOp",EDGE,"E73.right")])],"isStart":false});
            var sketch = newSketch(context, id + "F74", { "sketchPlane" : qUnion([Q0])});
            skLineSegment(sketch, "E74", {"start": v(107.42, 1124.48) * mm, "end": v(69.8, 1227.85) * mm});
            skLineSegment(sketch, "E75", {"start": v(69.8, 1227.85) * mm, "end": v(130.88, 1250.08) * mm});
            skLineSegment(sketch, "E76", {"start": v(130.88, 1250.08) * mm, "end": v(168.5, 1146.71) * mm});
            skLineSegment(sketch, "E77", {"start": v(168.5, 1146.71) * mm, "end": v(107.42, 1124.48) * mm});
            skSolve(sketch);
        }
        {
            var Q0;
            Q0 = qSketchRegion(id + "F74", true);
            extrude(context, id + "F75", {"entities" : qUnion([Q0]), "depth" : 35 * mm});
        }
        {
            var Q0;
            Q0=makeQuery(id+"F75.opExtrude","CAP_EDGE",EDGE,{"disambiguationData":[OSD([sQuery(id+"F74.wireOp",EDGE,"E77")])],"isStart":false});
            var Q1;
            Q1=makeQuery(id+"F75.opExtrude","SWEPT_EDGE",EDGE,{"disambiguationData":[OSD([sQuery(id+"F74.wireOp",EDGE,"E74"),sQuery(id+"F74.wireOp",EDGE,"E77")])]});
            var Q2;
            Q2=makeQuery(id+"F75.opExtrude","SWEPT_EDGE",EDGE,{"disambiguationData":[OSD([sQuery(id+"F74.wireOp",EDGE,"E76"),sQuery(id+"F74.wireOp",EDGE,"E77")])]});
            var Q3;
            Q3=makeQuery(id+"F75.opExtrude","CAP_EDGE",EDGE,{"disambiguationData":[OSD([sQuery(id+"F74.wireOp",EDGE,"E74")])],"isStart":false});
            var Q4;
            Q4=makeQuery(id+"F75.opExtrude","SWEPT_EDGE",EDGE,{"disambiguationData":[OSD([sQuery(id+"F74.wireOp",EDGE,"E74"),sQuery(id+"F74.wireOp",EDGE,"E75")])]});
            var Q5;
            Q5=makeQuery(id+"F75.opExtrude","CAP_EDGE",EDGE,{"disambiguationData":[OSD([sQuery(id+"F74.wireOp",EDGE,"E75")])],"isStart":false});
            var Q6;
            Q6=makeQuery(id+"F75.opExtrude","SWEPT_EDGE",EDGE,{"disambiguationData":[OSD([sQuery(id+"F74.wireOp",EDGE,"E75"),sQuery(id+"F74.wireOp",EDGE,"E76")])]});
            var Q7;
            Q7=makeQuery(id+"F75.opExtrude","CAP_EDGE",EDGE,{"disambiguationData":[OSD([sQuery(id+"F74.wireOp",EDGE,"E76")])],"isStart":false});
            fillet(context, id + "F76", {"entities" : qUnion([Q0, Q1, Q2, Q3, Q4, Q5, Q6, Q7]), "radius" : 20 * mm, "tangentPropagation" : true, "allowEdgeOverflow" : false});
        }
    });
